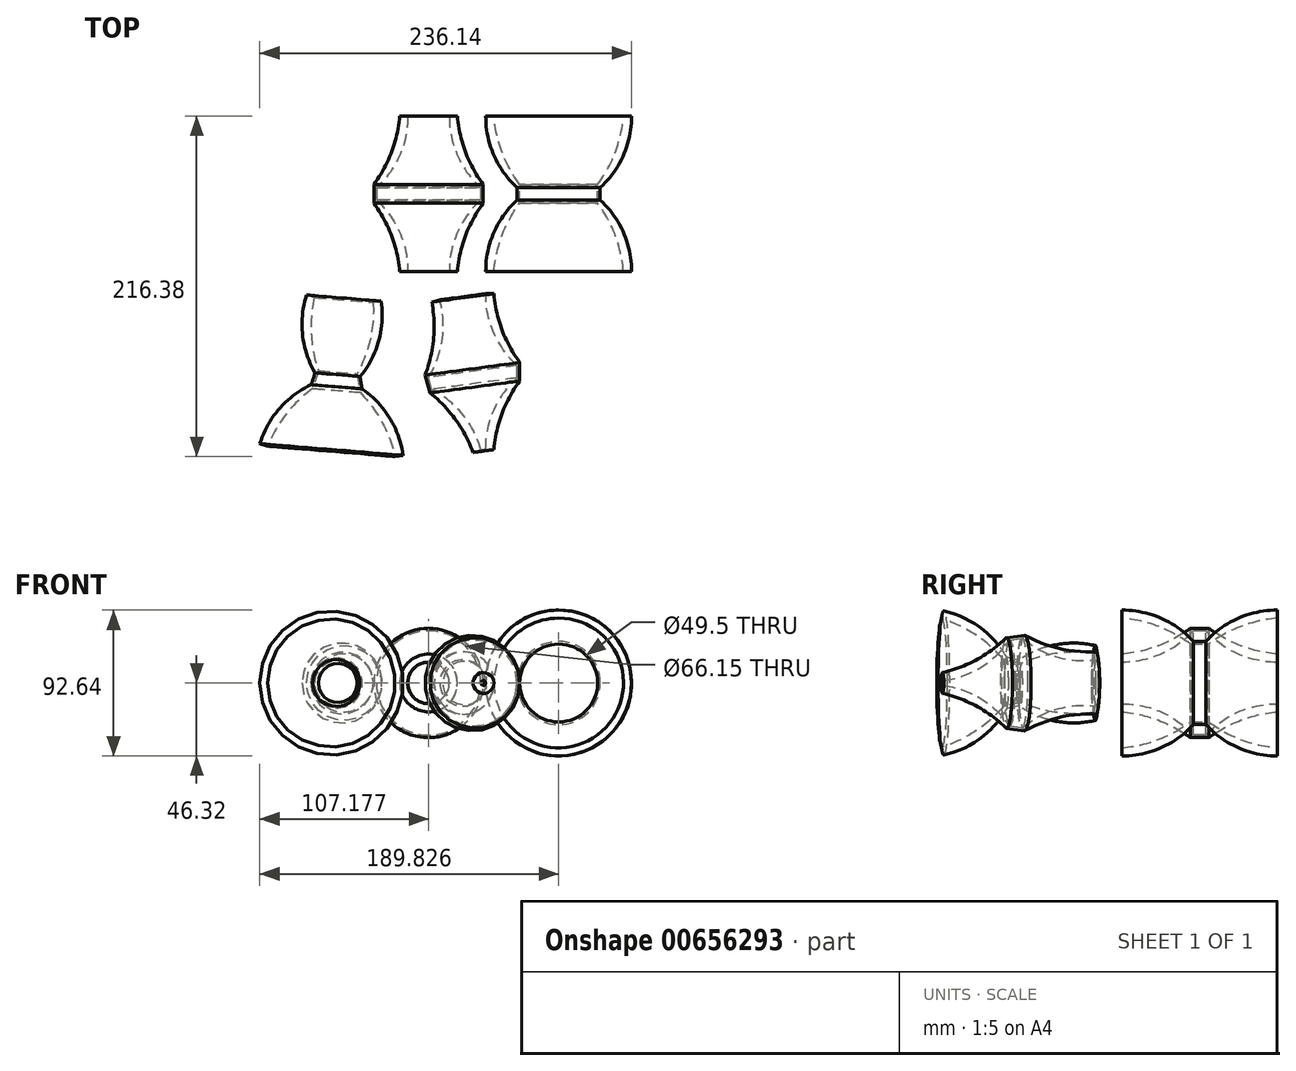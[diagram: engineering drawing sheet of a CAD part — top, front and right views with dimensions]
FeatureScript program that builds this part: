
annotation { "Feature Type Name" : "Feature", "Feature Type Description" : "" }
export const myFeature = defineFeature(function(context is Context, id is Id, definition is map)
    precondition{}
    {
        {
            var Q0;
            Q0=qCreatedBy(makeId("Top.planeOp"),FACE);
            var sketch = newSketch(context, id + "F0", { "sketchPlane" : qUnion([Q0])});
            skArc(sketch, "E0", {"start": v(-57.47, 16.42) * mm, "mid": v(-46.22, 37.09) * mm, "end": v(-41.05, 60.04) * mm});
            skLineSegment(sketch, "E1", {"start": v(-41.05, 60.04) * mm, "end": v(-35.9, 60.04) * mm});
            skArc(sketch, "E2", {"start": v(-55.8, 14.5) * mm, "mid": v(-41.03, 35.16) * mm, "end": v(-35.9, 60.04) * mm});
            skPoint(sketch, "E3.end.orphan", {"position": v(-55.8, 0) * mm});
            skLineSegment(sketch, "E4", {"start": v(-22.73, 0) * mm, "end": v(-22.73, 16.67) * mm});
            skLineSegment(sketch, "E5", {"start": v(-22.73, 16.67) * mm, "end": v(-55.8, 14.5) * mm});
            skLineSegment(sketch, "E6.MirrorCS", {"start": v(-41.05, -38.96) * mm, "end": v(-35.9, -38.96) * mm});
            skArc(sketch, "E7.MirrorCS", {"start": v(-57.47, 4.66) * mm, "mid": v(-46.22, -16.01) * mm, "end": v(-41.05, -38.96) * mm});
            skArc(sketch, "E8.MirrorCS", {"start": v(-55.8, 6.57) * mm, "mid": v(-41.03, -14.1) * mm, "end": v(-35.9, -38.96) * mm});
            skLineSegment(sketch, "E9", {"start": v(-55.8, 6.57) * mm, "end": v(-55.8, 14.5) * mm});
            skLineSegment(sketch, "E10", {"start": v(-57.47, 16.42) * mm, "end": v(-57.47, 4.66) * mm});
            skLineSegment(sketch, "E11", {"start": v(-11.15, 63.96) * mm, "end": v(-11.15, -44.84) * mm});
            skLineSegment(sketch, "E12.MirrorCS", {"start": v(18.75, -38.96) * mm, "end": v(13.6, -38.96) * mm});
            skLineSegment(sketch, "E13.MirrorCS", {"start": v(18.75, 60.04) * mm, "end": v(13.6, 60.04) * mm});
            skPoint(sketch, "E14.MirrorP", {"position": v(33.5, 0) * mm});
            skLineSegment(sketch, "E15.MirrorCS", {"start": v(35.17, 16.42) * mm, "end": v(35.17, 4.66) * mm});
            skLineSegment(sketch, "E16.MirrorCS", {"start": v(33.5, 6.57) * mm, "end": v(33.5, 14.5) * mm});
            skArc(sketch, "E17.MirrorCS", {"start": v(33.5, 6.57) * mm, "mid": v(18.73, -14.1) * mm, "end": v(13.6, -38.96) * mm});
            skArc(sketch, "E18.MirrorCS", {"start": v(33.5, 14.5) * mm, "mid": v(18.73, 35.16) * mm, "end": v(13.6, 60.04) * mm});
            skArc(sketch, "E19.MirrorCS", {"start": v(35.17, 4.66) * mm, "mid": v(23.92, -16.01) * mm, "end": v(18.75, -38.96) * mm});
            skArc(sketch, "E20.MirrorCS", {"start": v(35.17, 16.42) * mm, "mid": v(23.92, 37.09) * mm, "end": v(18.75, 60.04) * mm});
            skPoint(sketch, "E21.MirrorCS.start.orphan", {"position": v(0.43, 0) * mm});
            skPoint(sketch, "E22.MirrorCS.start.orphan", {"position": v(0.43, 16.67) * mm});
            skLineSegment(sketch, "E23", {"start": v(35.17, 16.42) * mm, "end": v(59.92, 16.42) * mm});
            skLineSegment(sketch, "E24", {"start": v(59.92, 16.42) * mm, "end": v(59.92, 0) * mm});
            skLineSegment(sketch, "E25", {"start": v(6.9, -45.93) * mm, "end": v(73.4, -45.93) * mm});
            skLineSegment(sketch, "E26.MirrorCS", {"start": v(35.17, -108.29) * mm, "end": v(35.17, -96.52) * mm});
            skLineSegment(sketch, "E27.MirrorCS", {"start": v(18.75, -151.9) * mm, "end": v(13.6, -151.9) * mm});
            skLineSegment(sketch, "E28.MirrorCS", {"start": v(18.75, -52.9) * mm, "end": v(13.6, -52.9) * mm});
            skLineSegment(sketch, "E29.MirrorCS", {"start": v(33.5, -98.43) * mm, "end": v(33.5, -106.38) * mm});
            skPoint(sketch, "E30.MirrorP", {"position": v(33.5, -91.87) * mm});
            skPoint(sketch, "E31.MirrorP", {"position": v(0.43, -108.53) * mm});
            skArc(sketch, "E32.MirrorCS", {"start": v(33.5, -106.38) * mm, "mid": v(18.73, -127.03) * mm, "end": v(13.6, -151.9) * mm});
            skArc(sketch, "E33.MirrorCS", {"start": v(35.17, -108.29) * mm, "mid": v(23.92, -128.95) * mm, "end": v(18.75, -151.9) * mm});
            skArc(sketch, "E34.MirrorCS", {"start": v(35.17, -96.52) * mm, "mid": v(23.92, -75.86) * mm, "end": v(18.75, -52.9) * mm});
            skArc(sketch, "E35.MirrorCS", {"start": v(33.5, -98.43) * mm, "mid": v(18.73, -77.78) * mm, "end": v(13.6, -52.9) * mm});
            skPoint(sketch, "E36.MirrorP", {"position": v(0.43, -91.87) * mm});
            skPoint(sketch, "E37.MirrorCS.end.orphan", {"position": v(59.92, -91.87) * mm});
            skPoint(sketch, "E37.MirrorCS.start.orphan", {"position": v(59.92, -108.29) * mm});
            skLineSegment(sketch, "E38", {"start": v(33.5, -98.43) * mm, "end": v(4.85, -98.43) * mm});
            skLineSegment(sketch, "E39", {"start": v(4.85, -98.43) * mm, "end": v(0, -62.46) * mm});
            skLineSegment(sketch, "E40", {"start": v(-19.99, -49.9) * mm, "end": v(-10.87, -178.73) * mm});
            skLineSegment(sketch, "E41.MirrorCS", {"start": v(-66.11, -105.49) * mm, "end": v(-65, -113.35) * mm});
            skLineSegment(sketch, "E42.MirrorCS", {"start": v(-66.36, -115.47) * mm, "end": v(-68.02, -103.83) * mm});
            skLineSegment(sketch, "E43.MirrorCS", {"start": v(-43.96, -156.34) * mm, "end": v(-38.87, -155.62) * mm});
            skLineSegment(sketch, "E44.MirrorCS", {"start": v(-57.91, -58.33) * mm, "end": v(-52.82, -57.6) * mm});
            skArc(sketch, "E45.MirrorCS", {"start": v(-66.11, -105.49) * mm, "mid": v(-54.4, -82.95) * mm, "end": v(-52.82, -57.6) * mm});
            skPoint(sketch, "E46.MirrorP", {"position": v(-31.94, -110.83) * mm});
            skArc(sketch, "E47.MirrorCS", {"start": v(-66.36, -115.47) * mm, "mid": v(-52.32, -134.35) * mm, "end": v(-43.96, -156.34) * mm});
            skArc(sketch, "E48.MirrorCS", {"start": v(-65, -113.35) * mm, "mid": v(-47.45, -131.72) * mm, "end": v(-38.87, -155.62) * mm});
            skPoint(sketch, "E49.MirrorP", {"position": v(-67.04, -98.99) * mm});
            skPoint(sketch, "E50.MirrorP", {"position": v(-34.3, -94.33) * mm});
            skArc(sketch, "E51.MirrorCS", {"start": v(-68.02, -103.83) * mm, "mid": v(-59.8, -81.78) * mm, "end": v(-57.91, -58.33) * mm});
            skPoint(sketch, "E52.end.orphan", {"position": v(-18.5, 0) * mm});
            skLineSegment(sketch, "E53", {"start": v(-71.94, 0) * mm, "end": v(-80.14, -100.05) * mm});
            skLineSegment(sketch, "E54", {"start": v(-80.14, -100.05) * mm, "end": v(-68.02, -103.83) * mm});
            skSolve(sketch);
        }
        {
            var Q0;
            Q0=makeQuery(id+"F0.imprint","IMPRINT",FACE,{"disambiguationData":[TD([[makeQuery(id+"F0.imprint","IMPRINT",EDGE,{"derivedFrom":sQuery(id+"F0.wireOp",EDGE,"E0")}),-1.0]])]});
            var Q1;
            Q1=sQuery(id+"F0.wireOp",EDGE,"E4");
            revolve(context, id + "F1", {"entities" : qUnion([Q0]), "axis" : qUnion([Q1]), "revolveType" : RevolveType.FULL});
        }
        {
            var Q0;
            Q0=makeQuery(id+"F0.imprint","IMPRINT",FACE,{"disambiguationData":[TD([[makeQuery(id+"F0.imprint","IMPRINT",EDGE,{"derivedFrom":sQuery(id+"F0.wireOp",EDGE,"E12.MirrorCS")}),-1.0]])]});
            var Q1;
            Q1=sQuery(id+"F0.wireOp",EDGE,"E24");
            revolve(context, id + "F2", {"entities" : qUnion([Q0]), "axis" : qUnion([Q1]), "revolveType" : RevolveType.FULL});
        }
        {
            var Q0;
            Q0=makeQuery(id+"F0.imprint","IMPRINT",FACE,{"disambiguationData":[TD([[makeQuery(id+"F0.imprint","IMPRINT",EDGE,{"derivedFrom":sQuery(id+"F0.wireOp",EDGE,"E26.MirrorCS")}),1.0]])]});
            var Q1;
            Q1=sQuery(id+"F0.wireOp",EDGE,"E39");
            revolve(context, id + "F3", {"entities" : qUnion([Q0]), "axis" : qUnion([Q1]), "revolveType" : RevolveType.FULL});
        }
        {
            var Q0;
            Q0=makeQuery(id+"F0.imprint","IMPRINT",FACE,{"disambiguationData":[TD([[makeQuery(id+"F0.imprint","IMPRINT",EDGE,{"derivedFrom":sQuery(id+"F0.wireOp",EDGE,"E41.MirrorCS")}),-1.0]])]});
            var Q1;
            Q1=sQuery(id+"F0.wireOp",EDGE,"E53");
            revolve(context, id + "F4", {"entities" : qUnion([Q0]), "axis" : qUnion([Q1]), "revolveType" : RevolveType.FULL});
        }
    });
